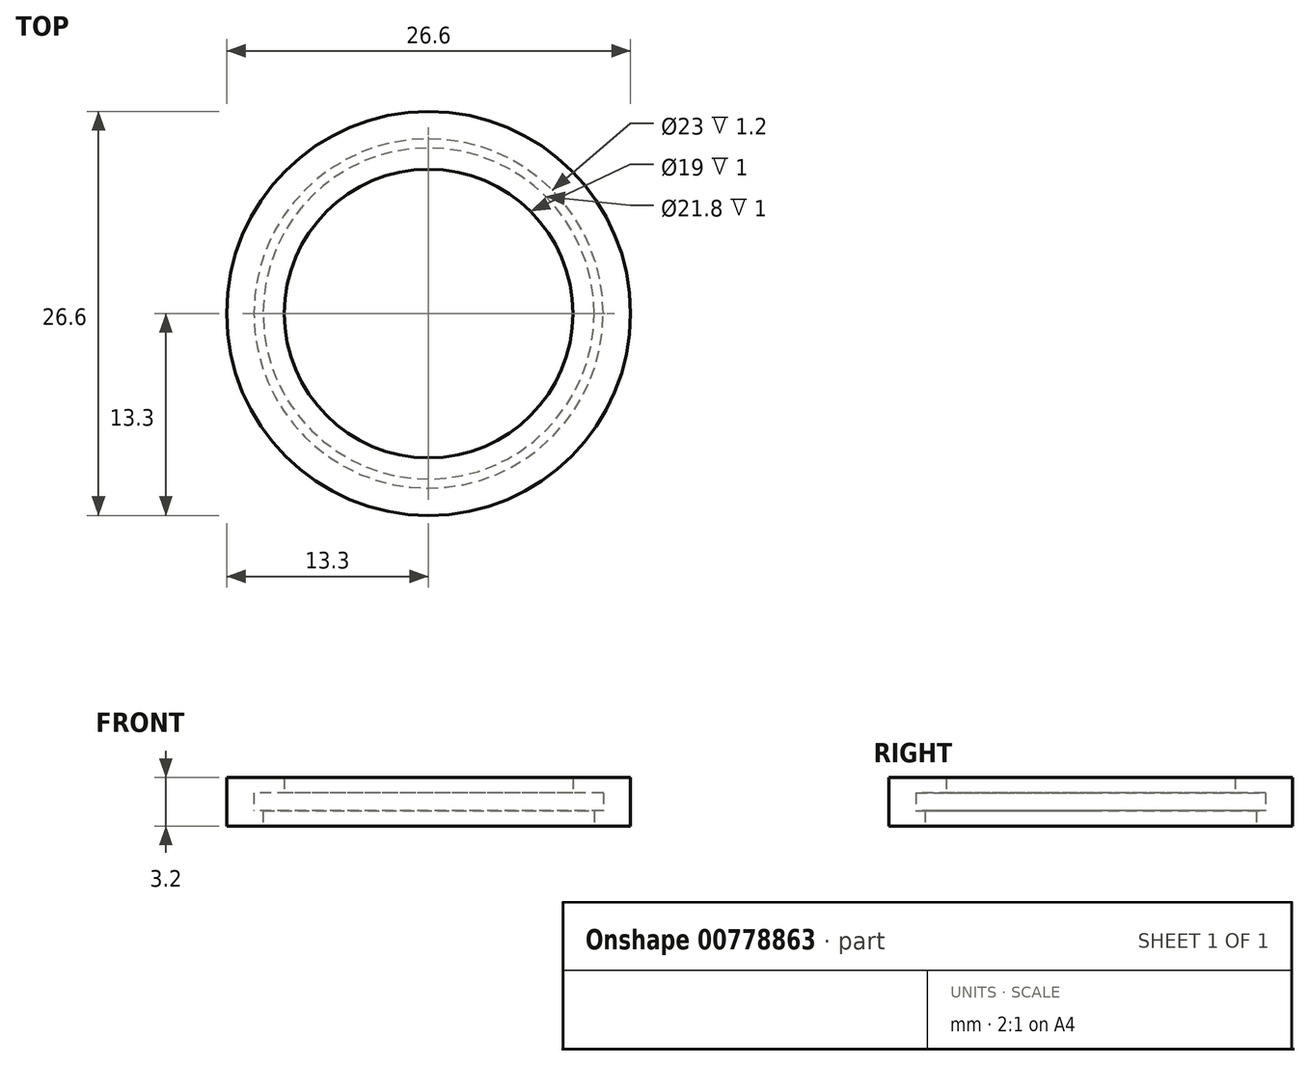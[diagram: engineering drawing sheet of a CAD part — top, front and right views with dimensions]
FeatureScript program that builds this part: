
annotation { "Feature Type Name" : "Feature", "Feature Type Description" : "" }
export const myFeature = defineFeature(function(context is Context, id is Id, definition is map)
    precondition{}
    {
        {
            var Q0;
            Q0=qCreatedBy(makeId("Top.planeOp"),FACE);
            var sketch = newSketch(context, id + "F0", { "sketchPlane" : qUnion([Q0])});
            skCircle(sketch, "E0", {"center": v(0, 0) * mm, "radius": 11.5 * mm});
            skCircle(sketch, "E1", {"center": v(0, 0) * mm, "radius": 13.3 * mm});
            skSolve(sketch);
        }
        {
            var Q0;
            Q0=makeQuery(id+"F0.imprint","IMPRINT",FACE,{"disambiguationData":[TD([[makeQuery(id+"F0.imprint","IMPRINT",EDGE,{"derivedFrom":sQuery(id+"F0.wireOp",EDGE,"E0")}),-1.0]])]});
            extrude(context, id + "F1", {"entities" : qUnion([Q0]), "depth" : 2.2 * mm, "offsetDistance" : 25 * mm});
        }
        {
            var Q0;
            Q0=makeQuery(id+"F1.opExtrude","CAP_FACE",FACE,{"disambiguationData":[OSD([sQuery(id+"F0.wireOp",EDGE,"E0"),sQuery(id+"F0.wireOp",EDGE,"E1")])],"isStart":false});
            var sketch = newSketch(context, id + "F2", { "sketchPlane" : qUnion([Q0])});
            skCircle(sketch, "E2", {"center": v(0, 0) * mm, "radius": 9.5 * mm});
            skSolve(sketch);
        }
        {
            var Q0;
            Q0=makeQuery(id+"F2.imprint","IMPRINT",FACE,{"disambiguationData":[TD([[makeQuery(id+"F2.imprint","IMPRINT",EDGE,{"derivedFrom":sQuery(id+"F2.wireOp",EDGE,"E2")}),-1.0]])]});
            var Q1;
            Q1=makeQuery(id+"F2.imprint","IMPRINT",FACE,{"disambiguationData":[TD([[makeQuery(id+"F2.imprint","IMPRINT",EDGE,{"derivedFrom":makeQuery(id+"F1.opExtrude","CAP_EDGE",EDGE,{"disambiguationData":[OSD([sQuery(id+"F0.wireOp",EDGE,"E0")])],"isStart":false})}),-1.0]])]});
            extrude(context, id + "F3", {"entities" : qUnion([Q0, Q1]), "operationType" : NewBodyOperationType.ADD, "depth" : 1 * mm, "offsetDistance" : 25 * mm});
        }
        {
            var Q0;
            Q0=makeQuery(id+"F1.opExtrude","CAP_FACE",FACE,{"disambiguationData":[OSD([sQuery(id+"F0.wireOp",EDGE,"E0"),sQuery(id+"F0.wireOp",EDGE,"E1")])],"isStart":true});
            var sketch = newSketch(context, id + "F4", { "sketchPlane" : qUnion([Q0])});
            skCircle(sketch, "E3", {"center": v(0, 0) * mm, "radius": 10.9 * mm});
            skSolve(sketch);
        }
        {
            var Q0;
            Q0=makeQuery(id+"F4.imprint","IMPRINT",FACE,{"disambiguationData":[TD([[makeQuery(id+"F4.imprint","IMPRINT",EDGE,{"derivedFrom":sQuery(id+"F4.wireOp",EDGE,"E3")}),-1.0]])]});
            extrude(context, id + "F5", {"entities" : qUnion([Q0]), "operationType" : NewBodyOperationType.ADD, "oppositeDirection" : true, "depth" : 1 * mm, "offsetDistance" : 25 * mm});
        }
    });
